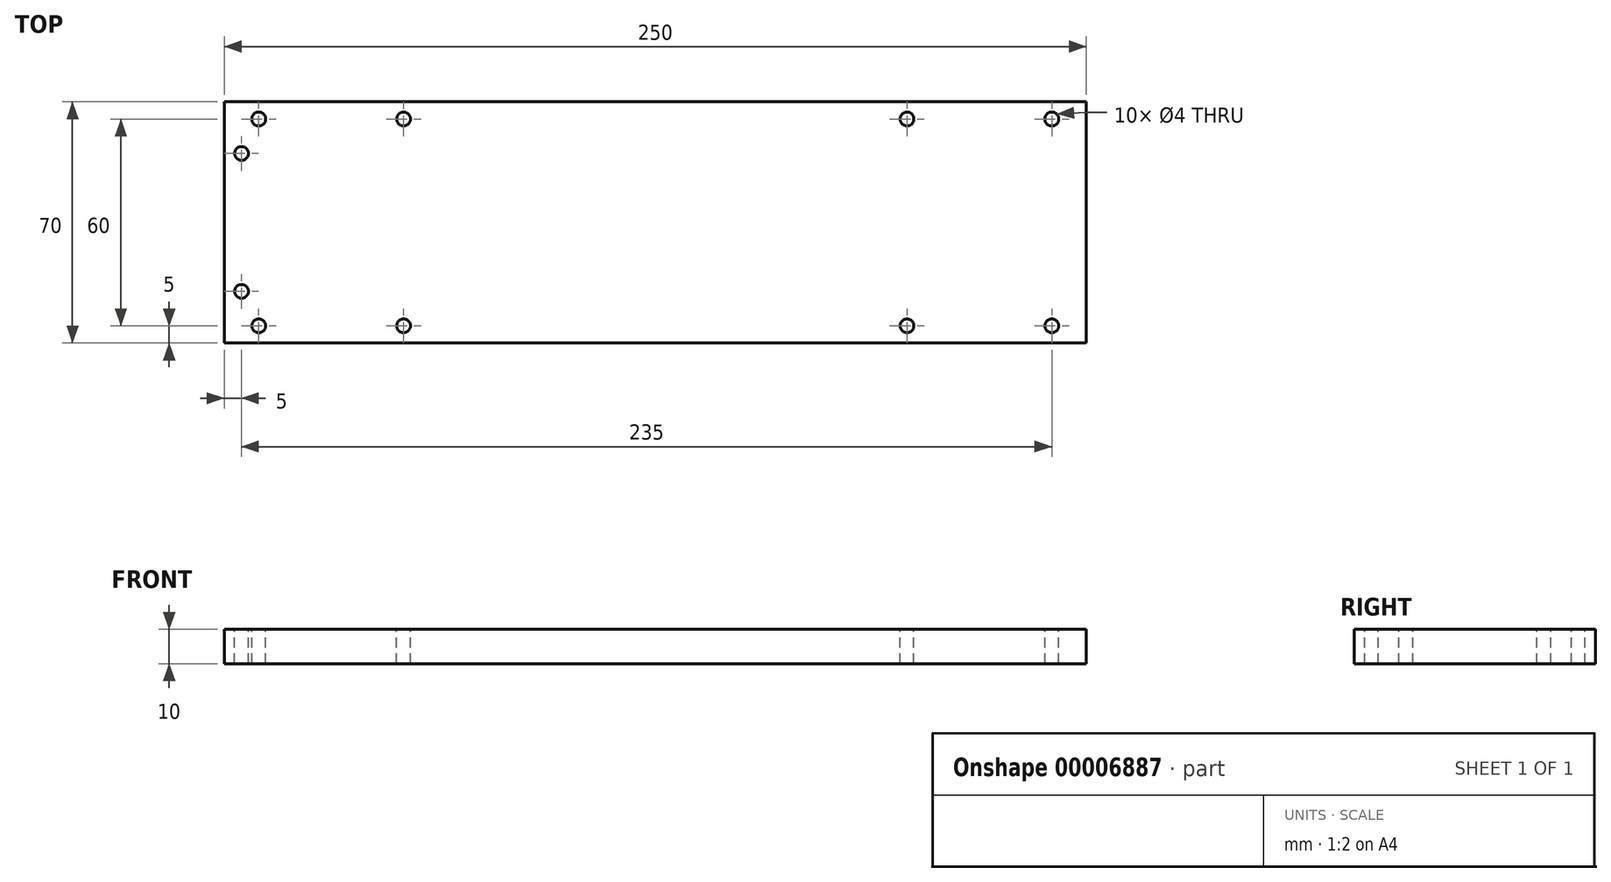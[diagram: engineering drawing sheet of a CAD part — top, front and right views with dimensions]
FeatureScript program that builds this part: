
annotation { "Feature Type Name" : "Feature", "Feature Type Description" : "" }
export const myFeature = defineFeature(function(context is Context, id is Id, definition is map)
    precondition{}
    {
        {
            var Q0;
            Q0=qCreatedBy(makeId("Top.planeOp"),FACE);
            var sketch = newSketch(context, id + "F0", { "sketchPlane" : qUnion([Q0])});
            skLineSegment(sketch, "E0.rect.bottom", {"start": v(150, -35) * mm, "end": v(-100, -35) * mm});
            skLineSegment(sketch, "E0.rect.top", {"start": v(150, 35) * mm, "end": v(-100, 35) * mm});
            skLineSegment(sketch, "E0.rect.left", {"start": v(150, -35) * mm, "end": v(150, 35) * mm});
            skLineSegment(sketch, "E0.rect.right", {"start": v(-100, -35) * mm, "end": v(-100, 35) * mm});
            skPoint(sketch, "E0.rect.middle", {"position": v(0, 0) * mm});
            skSolve(sketch);
        }
        {
            var Q0;
            {var subQ1=sQuery(id+"F0.wireOp",EDGE,"E0.rect.left");Q0=makeQuery(id+"F0.imprint","IMPRINT",FACE,{"disambiguationData":[TD([[makeQuery(id+"F0.imprint","IMPRINT",EDGE,{"derivedFrom":subQ1}),1.0]])]});}
            var Q1;
            {var subQ1=sQuery(id+"F0.wireOp",EDGE,"E0.rect.right");Q1=makeQuery(id+"F0.imprint","IMPRINT",FACE,{"disambiguationData":[TD([[makeQuery(id+"F0.imprint","IMPRINT",EDGE,{"derivedFrom":subQ1}),-1.0]])]});}
            extrude(context, id + "F1", {"entities" : qUnion([Q0, Q1]), "depth" : 10 * mm});
        }
        {
            var Q0;
            Q0=makeQuery(id+"F1.opExtrude","CAP_FACE",FACE,{"disambiguationData":[OSD([sQuery(id+"F0.wireOp",EDGE,"E0.rect.bottom"),sQuery(id+"F0.wireOp",EDGE,"E0.rect.top"),sQuery(id+"F0.wireOp",EDGE,"E0.rect.left"),sQuery(id+"F0.wireOp",EDGE,"E0.rect.right")])],"isStart":false});
            var sketch = newSketch(context, id + "F2", { "sketchPlane" : qUnion([Q0])});
            skLineSegment(sketch, "E1", {"start": v(-100, 30) * mm, "end": v(150, 30) * mm, "construction": true});
            skLineSegment(sketch, "E2", {"start": v(-100, -30) * mm, "end": v(150, -30) * mm, "construction": true});
            skCircle(sketch, "E3", {"center": v(-90, 30) * mm, "radius": 2 * mm});
            skCircle(sketch, "E4", {"center": v(-48, 30) * mm, "radius": 2 * mm});
            skCircle(sketch, "E5", {"center": v(-90, -30) * mm, "radius": 2 * mm});
            skCircle(sketch, "E6", {"center": v(-48, -30) * mm, "radius": 2 * mm});
            skCircle(sketch, "E7", {"center": v(140, 30) * mm, "radius": 2 * mm});
            skCircle(sketch, "E8", {"center": v(98, 30) * mm, "radius": 2 * mm});
            skCircle(sketch, "E9", {"center": v(98, -30) * mm, "radius": 2 * mm});
            skCircle(sketch, "E10", {"center": v(140, -30) * mm, "radius": 2 * mm});
            skLineSegment(sketch, "E11", {"start": v(150, -30) * mm, "end": v(-100, -30) * mm, "construction": true});
            skCircle(sketch, "E12", {"center": v(-95, 20) * mm, "radius": 2 * mm});
            skCircle(sketch, "E13", {"center": v(-95, -20) * mm, "radius": 2 * mm});
            skSolve(sketch);
        }
        {
            var Q0;
            Q0 = qSketchRegion(id + "F2", true);
            extrude(context, id + "F3", {"entities" : qUnion([Q0]), "operationType" : NewBodyOperationType.REMOVE, "endBound" : BoundingType.THROUGH_ALL, "oppositeDirection" : true, "depth" : 25 * mm});
        }
    });
